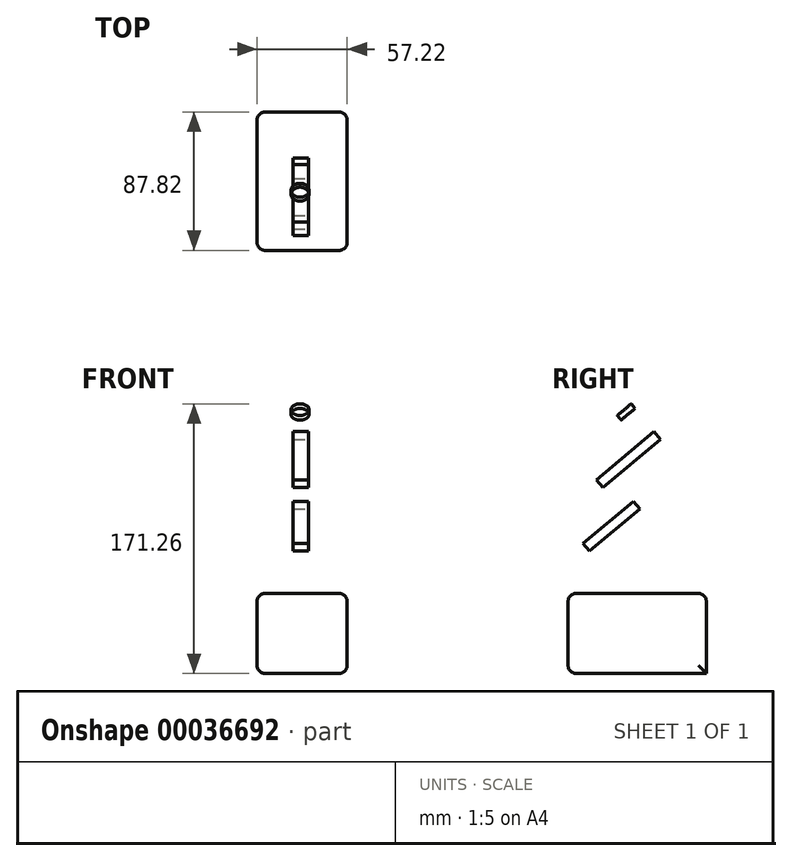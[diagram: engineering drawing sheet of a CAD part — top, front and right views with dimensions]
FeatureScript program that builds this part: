
annotation { "Feature Type Name" : "Feature", "Feature Type Description" : "" }
export const myFeature = defineFeature(function(context is Context, id is Id, definition is map)
    precondition{}
    {
        {
            var Q0;
            Q0=qCreatedBy(makeId("Top.planeOp"),FACE);
            var sketch = newSketch(context, id + "F0", { "sketchPlane" : qUnion([Q0])});
            skLineSegment(sketch, "E0.bottom", {"start": v(-22.95, 46.97) * mm, "end": v(34.27, 46.97) * mm});
            skLineSegment(sketch, "E0.top", {"start": v(-22.95, -40.85) * mm, "end": v(34.27, -40.85) * mm});
            skLineSegment(sketch, "E0.left", {"start": v(-22.95, 46.97) * mm, "end": v(-22.95, -40.85) * mm});
            skLineSegment(sketch, "E0.right", {"start": v(34.27, 46.97) * mm, "end": v(34.27, -40.85) * mm});
            skSolve(sketch);
        }
        {
            var Q0;
            Q0=makeQuery(id+"F0.imprint","IMPRINT",FACE,{"disambiguationData":[TD([[makeQuery(id+"F0.imprint","IMPRINT",EDGE,{"derivedFrom":sQuery(id+"F0.wireOp",EDGE,"E0.bottom")}),-1.0]])]});
            extrude(context, id + "F1", {"entities" : qUnion([Q0]), "depth" : 50.8 * mm});
        }
        {
            var Q0;
            Q0=makeQuery(id+"F1.opExtrude","SWEPT_FACE",FACE,{"disambiguationData":[OSD([sQuery(id+"F0.wireOp",EDGE,"E0.top")])]});
            var Q1;
            Q1=makeQuery(id+"F1.opExtrude","SWEPT_FACE",FACE,{"disambiguationData":[OSD([sQuery(id+"F0.wireOp",EDGE,"E0.right")])]});
            var Q2;
            Q2=makeQuery(id+"F1.opExtrude","CAP_FACE",FACE,{"disambiguationData":[OSD([sQuery(id+"F0.wireOp",EDGE,"E0.bottom"),sQuery(id+"F0.wireOp",EDGE,"E0.top"),sQuery(id+"F0.wireOp",EDGE,"E0.left"),sQuery(id+"F0.wireOp",EDGE,"E0.right")])],"isStart":false});
            var Q3;
            Q3=makeQuery(id+"F1.opExtrude","SWEPT_FACE",FACE,{"disambiguationData":[OSD([sQuery(id+"F0.wireOp",EDGE,"E0.left")])]});
            fillet(context, id + "F2", {"entities" : qUnion([Q0, Q1, Q2, Q3]), "radius" : 5.08 * mm, "tangentPropagation" : true, "allowEdgeOverflow" : false});
        }
        {
            var Q0;
            {var subQ0=sQuery(id+"F0.wireOp",EDGE,"E0.top");Q0=makeQuery(id+"F2.opFillet","BLEND_FACE",FACE,{"disambiguationData":[OSD([subQ0]),TDD([makeQuery(id+"F1.opExtrude","CAP_EDGE",EDGE,{"disambiguationData":[OSD([subQ0])],"isStart":false})])]});}
            cPlane(context, id + "F3", {"entities" : qUnion([Q0]), "cplaneType" : CPlaneType.LINE_ANGLE, "offset" : 152.4 * mm, "angle" : 50 * degree, "width" : 152.4 * mm, "height" : 152.4 * mm});
        }
        {
            var Q0;
            Q0=qCreatedBy(id+"F3.planeOp",FACE);
            cPlane(context, id + "F4", {"entities" : qUnion([Q0]), "cplaneType" : CPlaneType.OFFSET, "offset" : 19.05 * mm, "width" : 152.4 * mm, "height" : 152.4 * mm});
        }
        {
            var Q0;
            Q0=qCreatedBy(id+"F4.planeOp",FACE);
            var sketch = newSketch(context, id + "F5", { "sketchPlane" : qUnion([Q0])});
            skLineSegment(sketch, "E1.bottom", {"start": v(0, 29.12) * mm, "end": v(9.8, 29.12) * mm});
            skLineSegment(sketch, "E1.top", {"start": v(0, 70.81) * mm, "end": v(9.8, 70.81) * mm});
            skLineSegment(sketch, "E1.left", {"start": v(9.8, 29.12) * mm, "end": v(9.8, 70.81) * mm});
            skLineSegment(sketch, "E1.right", {"start": v(0, 29.12) * mm, "end": v(0, 70.81) * mm});
            skSolve(sketch);
        }
        {
            var Q0;
            Q0 = qSketchRegion(id + "F5", true);
            extrude(context, id + "F6", {"entities" : qUnion([Q0]), "operationType" : NewBodyOperationType.ADD, "depth" : 6.35 * mm});
        }
        {
            var Q0;
            Q0=makeQuery(id+"F6.opExtrude","CAP_FACE",FACE,{"disambiguationData":[OSD([sQuery(id+"F5.wireOp",EDGE,"E1.bottom"),sQuery(id+"F5.wireOp",EDGE,"E1.top"),sQuery(id+"F5.wireOp",EDGE,"E1.left"),sQuery(id+"F5.wireOp",EDGE,"E1.right")])],"isStart":false});
            cPlane(context, id + "F7", {"entities" : qUnion([Q0]), "cplaneType" : CPlaneType.OFFSET, "offset" : 19.05 * mm, "width" : 152.4 * mm, "height" : 152.4 * mm});
        }
        {
            var Q0;
            Q0=qCreatedBy(id+"F7.planeOp",FACE);
            var sketch = newSketch(context, id + "F8", { "sketchPlane" : qUnion([Q0])});
            skLineSegment(sketch, "E2.bottom", {"start": v(0, 61.61) * mm, "end": v(9.75, 61.61) * mm});
            skLineSegment(sketch, "E2.top", {"start": v(0, 109.32) * mm, "end": v(9.75, 109.32) * mm});
            skLineSegment(sketch, "E2.left", {"start": v(0, 61.61) * mm, "end": v(0, 109.32) * mm});
            skLineSegment(sketch, "E2.right", {"start": v(9.75, 61.61) * mm, "end": v(9.75, 109.32) * mm});
            skSolve(sketch);
        }
        {
            var Q0;
            Q0 = qSketchRegion(id + "F8", true);
            extrude(context, id + "F9", {"entities" : qUnion([Q0]), "operationType" : NewBodyOperationType.ADD, "depth" : 6.35 * mm});
        }
        {
            var Q0;
            Q0=makeQuery(id+"F9.opExtrude","CAP_FACE",FACE,{"disambiguationData":[OSD([sQuery(id+"F8.wireOp",EDGE,"E2.bottom"),sQuery(id+"F8.wireOp",EDGE,"E2.top"),sQuery(id+"F8.wireOp",EDGE,"E2.left"),sQuery(id+"F8.wireOp",EDGE,"E2.right")])],"isStart":false});
            cPlane(context, id + "F10", {"entities" : qUnion([Q0]), "cplaneType" : CPlaneType.OFFSET, "offset" : 19.05 * mm, "width" : 152.4 * mm, "height" : 152.4 * mm});
        }
        {
            var Q0;
            Q0=qCreatedBy(id+"F10.planeOp",FACE);
            var sketch = newSketch(context, id + "F11", { "sketchPlane" : qUnion([Q0])});
            skCircle(sketch, "E3", {"center": v(4.32, 103.76) * mm, "radius": 5.76 * mm});
            skSolve(sketch);
        }
        {
            var Q0;
            Q0 = qSketchRegion(id + "F11", true);
            extrude(context, id + "F12", {"entities" : qUnion([Q0]), "operationType" : NewBodyOperationType.ADD, "depth" : 3.8 * mm});
        }
        {
            var Q0;
            Q0=makeQuery(id+"F12.opExtrude","CAP_FACE",FACE,{"disambiguationData":[OSD([sQuery(id+"F11.wireOp",EDGE,"E3")])],"isStart":false});
            shell(context, id + "F13", {"entities" : qUnion([Q0]), "thickness" : 0.03 * mm});
        }
        {
            var Q0;
            Q0 = qSketchRegion(id + "F11", true);
            extrude(context, id + "F14", {"entities" : qUnion([Q0]), "operationType" : NewBodyOperationType.ADD, "depth" : 0.03 * mm});
        }
    });
